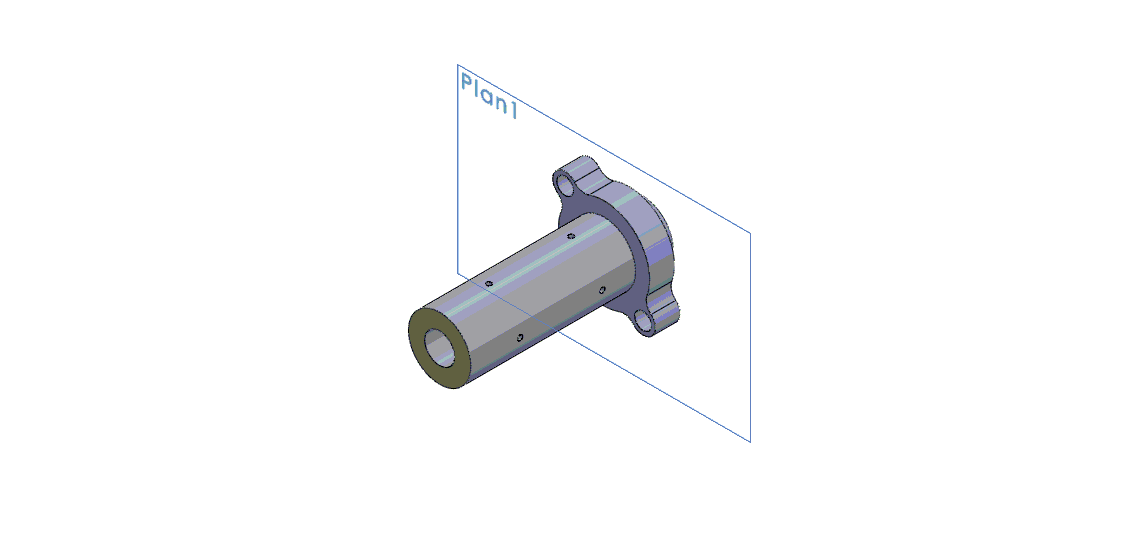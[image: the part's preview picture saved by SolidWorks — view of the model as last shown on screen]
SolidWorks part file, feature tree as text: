
SOLIDWORKS PART (.sldprt)
format: sldprt  version: not decoded by parser v0  size: 204,800 bytes
history: native  units: mm
features: sketch x6, plane x4, cut_extrude x4, extrude x2, material x1 (+10 scaffold rows collapsed)
feature tree (27):
  scaffold x10  (default folders/planes/origin — collapsed)
  material  "Matériau <non spécifié>"
  plane  "FRONT"
  plane  "TOP"
  plane  "RIGHT"
  plane  "Plan1"  Offset=838.2mm
  sketch  "Esquisse1"  dims[D2=~3.520382mm D1=67.0mm]
  extrude  "Boss.-Extru.1"  Depth=15mm
  sketch  "Esquisse9"  dims[D1=~8.950813mm]
  extrude  "Boss.-Extru.4"  Depth=100mm
  sketch  "Esquisse12"  dims[D1=~6.616621mm]
  cut_extrude  "Enlèv. mat.-Extru.2"  [1 undecoded]
  sketch  "Esquisse13"  dims[D1=~4.891676mm]
  cut_extrude  "Enlèv. mat.-Extru.3"  Depth=7mm
  sketch  "Esquisse14"  dims[D1=20.0mm D2=50.0mm]
  cut_extrude  "Enlèv. mat.-Extru.4"  Depth=7mm
  sketch  "Esquisse15"  dims[D1=20.0mm D2=50.0mm]
  cut_extrude  "Enlèv. mat.-Extru.5"  Depth=7mm
decode coverage: 11 of 12 modeling features carry decoded parameters
note: ~ marks probable driven/reference dimensions
note: 1 parameter value undecoded
note: suppression state not decoded; provenance and decode notes live in map.json
